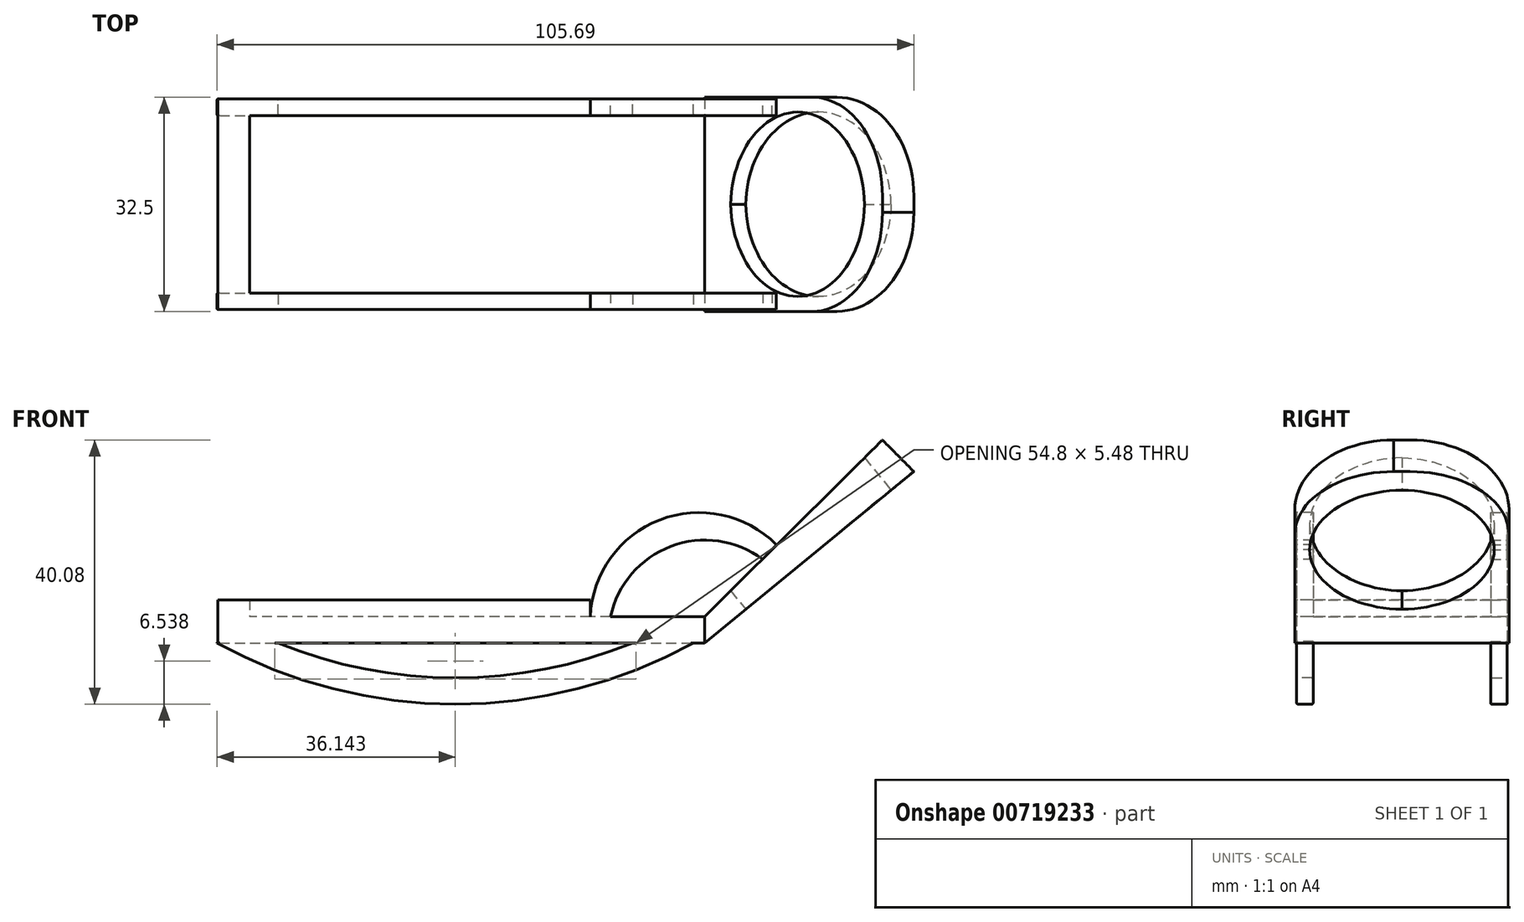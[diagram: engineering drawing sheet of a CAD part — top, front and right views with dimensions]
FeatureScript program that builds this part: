
annotation { "Feature Type Name" : "Feature", "Feature Type Description" : "" }
export const myFeature = defineFeature(function(context is Context, id is Id, definition is map)
    precondition{}
    {
        {
            var Q0;
            Q0=qCreatedBy(makeId("Top.planeOp"),FACE);
            var sketch = newSketch(context, id + "F0", { "sketchPlane" : qUnion([Q0])});
            skLineSegment(sketch, "E0.bottom", {"start": v(36.93, 15.97) * mm, "end": v(-36.93, 15.97) * mm});
            skLineSegment(sketch, "E0.top", {"start": v(36.93, -15.97) * mm, "end": v(-36.93, -15.97) * mm});
            skLineSegment(sketch, "E0.left", {"start": v(36.93, 15.97) * mm, "end": v(36.93, -15.97) * mm});
            skLineSegment(sketch, "E0.right", {"start": v(-36.93, 15.97) * mm, "end": v(-36.93, -15.97) * mm});
            skPoint(sketch, "E0.middle", {"position": v(0, 0) * mm});
            skSolve(sketch);
        }
        {
            var Q0;
            Q0 = qSketchRegion(id + "F0", true);
            extrude(context, id + "F1", {"entities" : qUnion([Q0]), "depth" : 4 * mm, "offsetDistance" : 25.4 * mm});
        }
        {
            var Q0;
            Q0=makeQuery(id+"F1.opExtrude","SWEPT_FACE",FACE,{"disambiguationData":[OSD([sQuery(id+"F0.wireOp",EDGE,"E0.top")])]});
            var sketch = newSketch(context, id + "F2", { "sketchPlane" : qUnion([Q0])});
            skLineSegment(sketch, "E1", {"start": v(36.93, 4) * mm, "end": v(63.87, 30.8) * mm});
            skLineSegment(sketch, "E2", {"start": v(63.87, 30.8) * mm, "end": v(68.62, 26.02) * mm});
            skLineSegment(sketch, "E3", {"start": v(68.62, 26.02) * mm, "end": v(36.93, 0) * mm});
            skLineSegment(sketch, "E4", {"start": v(36.93, 4) * mm, "end": v(33.19, 4) * mm});
            skLineSegment(sketch, "E5", {"start": v(33.19, 4) * mm, "end": v(33.19, 0) * mm});
            skLineSegment(sketch, "E6", {"start": v(33.19, 0) * mm, "end": v(36.93, 0) * mm});
            skSolve(sketch);
        }
        {
            var Q0;
            Q0=makeQuery(id+"F2.imprint","IMPRINT",FACE,{"disambiguationData":[TD([[makeQuery(id+"F2.imprint","IMPRINT",EDGE,{"derivedFrom":sQuery(id+"F2.wireOp",EDGE,"E1")}),-1.0]])]});
            extrude(context, id + "F3", {"entities" : qUnion([Q0]), "operationType" : NewBodyOperationType.ADD, "oppositeDirection" : true, "depth" : 32.22 * mm, "offsetDistance" : 25.4 * mm});
        }
        {
            var Q0;
            Q0=makeQuery(id+"F3.opExtrude","CAP_EDGE",EDGE,{"disambiguationData":[OSD([sQuery(id+"F2.wireOp",EDGE,"E2")])],"isStart":true});
            var Q1;
            Q1=makeQuery(id+"F3.opExtrude","CAP_EDGE",EDGE,{"disambiguationData":[OSD([sQuery(id+"F2.wireOp",EDGE,"E2")])],"isStart":false});
            fillet(context, id + "F4", {"entities" : qUnion([Q0, Q1]), "radius" : 15 * mm, "tangentPropagation" : true, "allowEdgeOverflow" : false});
        }
        {
            var Q0;
            Q0=makeQuery(id+"F3.opExtrude","SWEPT_FACE",FACE,{"disambiguationData":[OSD([sQuery(id+"F2.wireOp",EDGE,"E3")])]});
            var sketch = newSketch(context, id + "F5", { "sketchPlane" : qUnion([Q0])});
            skCircle(sketch, "E7", {"center": v(50.84, -0.25) * mm, "radius": 14.25 * mm});
            skPoint(sketch, "E7.first.point", {"position": v(60.93, 9.8) * mm});
            skPoint(sketch, "E7.second.point", {"position": v(40.58, -10.15) * mm});
            skPoint(sketch, "E7.third.point", {"position": v(54.48, -14.03) * mm});
            skSolve(sketch);
        }
        {
            var Q0;
            Q0=makeQuery(id+"F5.imprint","IMPRINT",FACE,{"disambiguationData":[TD([[makeQuery(id+"F5.imprint","IMPRINT",EDGE,{"derivedFrom":sQuery(id+"F5.wireOp",EDGE,"E7")}),1.0]])]});
            var sketch = newSketch(context, id + "F6", { "sketchPlane" : qUnion([Q0])});
            skSolve(sketch);
        }
        {
            var Q0;
            Q0=makeQuery(id+"F6.imprint","IMPRINT",FACE,{"disambiguationData":[TD([[makeQuery(id+"F6.imprint","IMPRINT",EDGE,{"derivedFrom":makeQuery(id+"F5.imprint","IMPRINT",EDGE,{"derivedFrom":sQuery(id+"F5.wireOp",EDGE,"E7")})}),1.0]])]});
            extrude(context, id + "F7", {"entities" : qUnion([Q0]), "operationType" : NewBodyOperationType.REMOVE, "oppositeDirection" : true, "depth" : 25.4 * mm, "offsetDistance" : 25.4 * mm});
        }
        {
            var Q0;
            {var subQ0=sQuery(id+"F0.wireOp",EDGE,"E0.top");Q0=makeQuery(id+"FbsTUUbUxmuc4po_1.boolean.opBoolean","MERGE",FACE,{"derivedFrom":[makeQuery(id+"F3.boolean.opBoolean","MERGE",FACE,{"derivedFrom":[makeQuery(id+"F1.opExtrude","SWEPT_FACE",FACE,{"disambiguationData":[OSD([subQ0])]}),makeQuery(id+"F3.opExtrude","CAP_FACE",FACE,{"disambiguationData":[OSD([subQ0,sQuery(id+"F0.wireOp",EDGE,"E0.left"),sQuery(id+"F2.wireOp",EDGE,"E1"),sQuery(id+"F2.wireOp",EDGE,"E2"),sQuery(id+"F2.wireOp",EDGE,"E3")])],"isStart":true})]}),makeQuery(id+"FbsTUUbUxmuc4po_1.opExtrude","CAP_FACE",FACE,{"disambiguationData":[OSD([sQuery(id+"F3iLMyL7hhnnokL_1.wireOp",EDGE,"af737c35-50d7-4836-b408-bd1f705a132f"),sQuery(id+"F3iLMyL7hhnnokL_1.wireOp",EDGE,"3ld4MRtO-RxEG-H6BP-Px8M-ibXYSdrbY1SH"),sQuery(id+"F3iLMyL7hhnnokL_1.wireOp",EDGE,"wHyz0mVY-Lv4J-rvW1-TTF2-0jSQOt01kzma")])],"isStart":true})]});}
            var sketch = newSketch(context, id + "F8", { "sketchPlane" : qUnion([Q0])});
            skArc(sketch, "E8.0", {"start": v(45.9, 12.56) * mm, "mid": v(31.65, 14.61) * mm, "end": v(22.51, 3.48) * mm});
            skLineSegment(sketch, "E9", {"start": v(45.9, 12.56) * mm, "end": v(47.74, 14.93) * mm});
            skLineSegment(sketch, "E10", {"start": v(22.51, 3.48) * mm, "end": v(19.56, 4) * mm});
            skArc(sketch, "E11", {"start": v(47.74, 14.93) * mm, "mid": v(30.08, 18.67) * mm, "end": v(19.56, 4) * mm});
            skSolve(sketch);
        }
        {
            var Q0;
            {var subQ0=sQuery(id+"F8.wireOp",EDGE,"E11");Q0=makeQuery(id+"F8.imprint","IMPRINT",FACE,{"disambiguationData":[TD([[makeQuery(id+"F8.imprint","IMPRINT",EDGE,{"derivedFrom":subQ0}),1.0]])]});}
            extrude(context, id + "F9", {"entities" : qUnion([Q0]), "operationType" : NewBodyOperationType.ADD, "oppositeDirection" : true, "depth" : 2.5 * mm, "offsetDistance" : 25.4 * mm});
        }
        {
            var Q0;
            Q0=makeQuery(id+"F1.opExtrude","SWEPT_BODY",BODY,{"disambiguationData":[OSD([sQuery(id+"F0.wireOp",EDGE,"E0.bottom"),sQuery(id+"F0.wireOp",EDGE,"E0.top"),sQuery(id+"F0.wireOp",EDGE,"E0.left"),sQuery(id+"F0.wireOp",EDGE,"E0.right")])]});
            var Q1;
            Q1=qCreatedBy(makeId("Front.planeOp"),FACE);
            mirror(context, id + "F10", {"operationType" : NewBodyOperationType.ADD, "entities" : qUnion([Q0]), "mirrorPlane" : qUnion([Q1])});
        }
        {
            var Q0;
            {var subQ0=sQuery(id+"F2.wireOp",EDGE,"E5");Q0=makeQuery(id+"F2.imprint","IMPRINT",FACE,{"disambiguationData":[TD([[makeQuery(id+"F2.imprint","IMPRINT",EDGE,{"derivedFrom":subQ0}),-1.0]])]});}
            var sketch = newSketch(context, id + "F11", { "sketchPlane" : qUnion([Q0])});
            skArc(sketch, "E12", {"start": v(-37.07, 0) * mm, "mid": v(-0.93, -9.28) * mm, "end": v(35.21, 0) * mm});
            skArc(sketch, "E13.0", {"start": v(-35.14, 3.5) * mm, "mid": v(-0.93, -5.28) * mm, "end": v(33.29, 3.5) * mm});
            skLineSegment(sketch, "E14", {"start": v(33.29, 3.5) * mm, "end": v(35.21, 0) * mm});
            skLineSegment(sketch, "E15", {"start": v(-35.14, 3.5) * mm, "end": v(-37.07, 0) * mm});
            skSolve(sketch);
        }
        {
            var Q0;
            Q0 = qSketchRegion(id + "F11", true);
            extrude(context, id + "F12", {"entities" : qUnion([Q0]), "operationType" : NewBodyOperationType.ADD, "oppositeDirection" : true, "depth" : 2.5 * mm, "offsetDistance" : 25.4 * mm});
        }
        {
            var Q0;
            Q0=makeQuery(id+"F12.opExtrude","CAP_EDGE",EDGE,{"disambiguationData":[OSD([sQuery(id+"F11.wireOp",EDGE,"E12")])],"isStart":true});
            var Q1;
            Q1=makeQuery(id+"F12.opExtrude","CAP_EDGE",EDGE,{"disambiguationData":[OSD([sQuery(id+"F11.wireOp",EDGE,"E12")])],"isStart":false});
            var Q2;
            Q2=makeQuery(id+"F12.opExtrude","CAP_EDGE",EDGE,{"disambiguationData":[OSD([sQuery(id+"F11.wireOp",EDGE,"E13.0")])],"isStart":true});
            var Q3;
            Q3=makeQuery(id+"F12.opExtrude","CAP_EDGE",EDGE,{"disambiguationData":[OSD([sQuery(id+"F11.wireOp",EDGE,"E13.0")])],"isStart":false});
            fillet(context, id + "F13", {"entities" : qUnion([Q0, Q1, Q2, Q3]), "radius" : 0.2 * mm, "tangentPropagation" : true, "allowEdgeOverflow" : false});
        }
        {
            var Q0;
            Q0=makeQuery(id+"F1.opExtrude","SWEPT_BODY",BODY,{"disambiguationData":[OSD([sQuery(id+"F0.wireOp",EDGE,"E0.bottom"),sQuery(id+"F0.wireOp",EDGE,"E0.top"),sQuery(id+"F0.wireOp",EDGE,"E0.left"),sQuery(id+"F0.wireOp",EDGE,"E0.right")])]});
            var Q1;
            Q1=qCreatedBy(makeId("Front.planeOp"),FACE);
            mirror(context, id + "F14", {"operationType" : NewBodyOperationType.ADD, "entities" : qUnion([Q0]), "mirrorPlane" : qUnion([Q1])});
        }
        {
            var Q0;
            Q0=makeQuery(id+"F1.opExtrude","CAP_FACE",FACE,{"disambiguationData":[OSD([sQuery(id+"F0.wireOp",EDGE,"E0.bottom"),sQuery(id+"F0.wireOp",EDGE,"E0.top"),sQuery(id+"F0.wireOp",EDGE,"E0.left"),sQuery(id+"F0.wireOp",EDGE,"E0.right")])],"isStart":false});
            var sketch = newSketch(context, id + "F15", { "sketchPlane" : qUnion([Q0])});
            skLineSegment(sketch, "E16.bottom", {"start": v(19.56, -13.47) * mm, "end": v(-36.93, -13.47) * mm});
            skLineSegment(sketch, "E16.top", {"start": v(19.56, -15.97) * mm, "end": v(-36.93, -15.97) * mm});
            skLineSegment(sketch, "E16.left", {"start": v(19.56, -13.47) * mm, "end": v(19.56, -15.97) * mm});
            skLineSegment(sketch, "E16.right", {"start": v(-36.93, -13.47) * mm, "end": v(-36.93, -15.97) * mm});
            skSolve(sketch);
        }
        {
            var Q0;
            Q0 = qSketchRegion(id + "F15", true);
            extrude(context, id + "F16", {"entities" : qUnion([Q0]), "operationType" : NewBodyOperationType.ADD, "depth" : 2.5 * mm, "offsetDistance" : 25.4 * mm});
        }
        {
            var Q0;
            Q0=makeQuery(id+"F1.opExtrude","CAP_FACE",FACE,{"disambiguationData":[OSD([sQuery(id+"F0.wireOp",EDGE,"E0.bottom"),sQuery(id+"F0.wireOp",EDGE,"E0.top"),sQuery(id+"F0.wireOp",EDGE,"E0.left"),sQuery(id+"F0.wireOp",EDGE,"E0.right")])],"isStart":false});
            var sketch = newSketch(context, id + "F17", { "sketchPlane" : qUnion([Q0])});
            skLineSegment(sketch, "E17.bottom", {"start": v(19.56, 15.97) * mm, "end": v(-36.93, 15.97) * mm});
            skLineSegment(sketch, "E17.top", {"start": v(19.56, 13.47) * mm, "end": v(-36.93, 13.47) * mm});
            skLineSegment(sketch, "E17.left", {"start": v(19.56, 15.97) * mm, "end": v(19.56, 13.47) * mm});
            skLineSegment(sketch, "E17.right", {"start": v(-36.93, 15.97) * mm, "end": v(-36.93, 13.47) * mm});
            skSolve(sketch);
        }
        {
            var Q0;
            Q0 = qSketchRegion(id + "F17", true);
            extrude(context, id + "F18", {"entities" : qUnion([Q0]), "operationType" : NewBodyOperationType.ADD, "depth" : 2.5 * mm, "offsetDistance" : 25.4 * mm});
        }
        {
            var Q0;
            Q0=makeQuery(id+"F1.opExtrude","CAP_FACE",FACE,{"disambiguationData":[OSD([sQuery(id+"F0.wireOp",EDGE,"E0.bottom"),sQuery(id+"F0.wireOp",EDGE,"E0.top"),sQuery(id+"F0.wireOp",EDGE,"E0.left"),sQuery(id+"F0.wireOp",EDGE,"E0.right")])],"isStart":false});
            var sketch = newSketch(context, id + "F19", { "sketchPlane" : qUnion([Q0])});
            skLineSegment(sketch, "E18.bottom", {"start": v(-36.93, -13.47) * mm, "end": v(-32.15, -13.47) * mm});
            skLineSegment(sketch, "E18.top", {"start": v(-36.93, 13.47) * mm, "end": v(-32.15, 13.47) * mm});
            skLineSegment(sketch, "E18.left", {"start": v(-36.93, -13.47) * mm, "end": v(-36.93, 13.47) * mm});
            skLineSegment(sketch, "E18.right", {"start": v(-32.15, -13.47) * mm, "end": v(-32.15, 13.47) * mm});
            skLineSegment(sketch, "E19.bottom", {"start": v(-34.54, 13.47) * mm, "end": v(-36.93, 13.47) * mm});
            skLineSegment(sketch, "E19.top", {"start": v(-34.54, -13.47) * mm, "end": v(-36.93, -13.47) * mm});
            skLineSegment(sketch, "E19.left", {"start": v(-34.54, 13.47) * mm, "end": v(-34.54, -13.47) * mm});
            skLineSegment(sketch, "E19.right", {"start": v(-36.93, 13.47) * mm, "end": v(-36.93, -13.47) * mm});
            skSolve(sketch);
        }
        {
            var Q0;
            Q0 = qSketchRegion(id + "F19", true);
            extrude(context, id + "F20", {"entities" : qUnion([Q0]), "operationType" : NewBodyOperationType.ADD, "depth" : 2.5 * mm, "offsetDistance" : 25.4 * mm});
        }
    });
